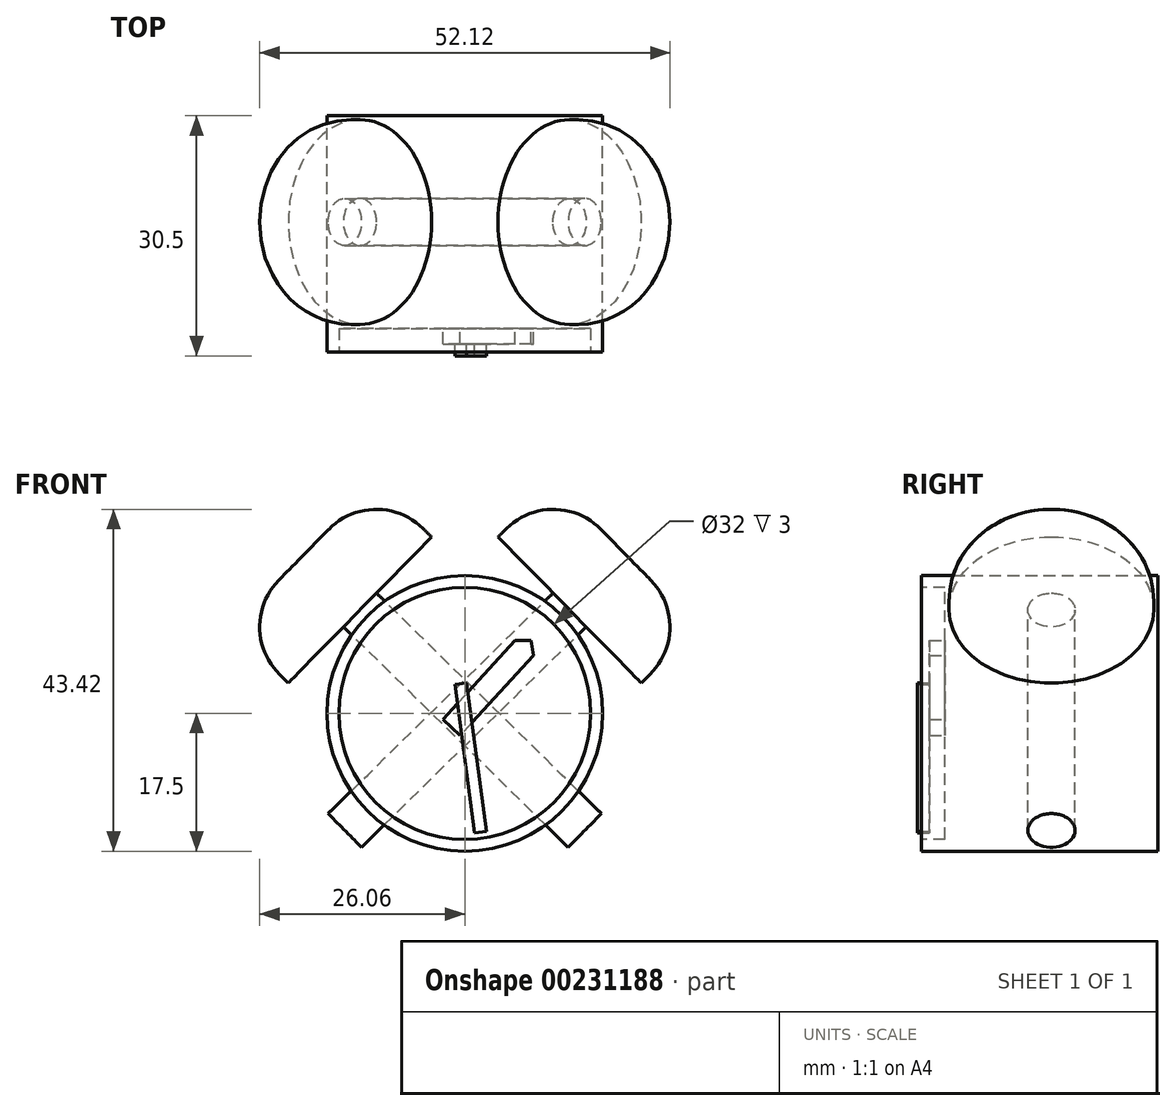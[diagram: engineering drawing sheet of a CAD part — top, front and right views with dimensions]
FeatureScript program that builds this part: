
annotation { "Feature Type Name" : "Feature", "Feature Type Description" : "" }
export const myFeature = defineFeature(function(context is Context, id is Id, definition is map)
    precondition{}
    {
        {
            var Q0;
            Q0=qCreatedBy(makeId("Front.planeOp"),FACE);
            var sketch = newSketch(context, id + "F0", { "sketchPlane" : qUnion([Q0])});
            skCircle(sketch, "E0", {"center": v(0, 0) * mm, "radius": 17.5 * mm});
            skSolve(sketch);
        }
        {
            var Q0;
            Q0=makeQuery(id+"F0.imprint","IMPRINT",FACE,{"disambiguationData":[TD([[makeQuery(id+"F0.imprint","IMPRINT",EDGE,{"derivedFrom":sQuery(id+"F0.wireOp",EDGE,"E0")}),1.0]])]});
            extrude(context, id + "F1", {"entities" : qUnion([Q0]), "depth" : 30 * mm});
        }
        {
            var Q0;
            Q0=makeQuery(id+"F1.opExtrude","CAP_FACE",FACE,{"disambiguationData":[OSD([sQuery(id+"F0.wireOp",EDGE,"E0")])],"isStart":false});
            var sketch = newSketch(context, id + "F2", { "sketchPlane" : qUnion([Q0])});
            skCircle(sketch, "E1", {"center": v(0, 0) * mm, "radius": 16 * mm});
            skSolve(sketch);
        }
        {
            var Q0;
            Q0=makeQuery(id+"F2.imprint","IMPRINT",FACE,{"disambiguationData":[TD([[makeQuery(id+"F2.imprint","IMPRINT",EDGE,{"derivedFrom":sQuery(id+"F2.wireOp",EDGE,"E1")}),1.0]])]});
            extrude(context, id + "F3", {"entities" : qUnion([Q0]), "operationType" : NewBodyOperationType.REMOVE, "oppositeDirection" : true, "depth" : 3 * mm});
        }
        {
            var Q0;
            Q0=makeQuery(id+"F1.opExtrude","CAP_FACE",FACE,{"disambiguationData":[OSD([sQuery(id+"F0.wireOp",EDGE,"E0")])],"isStart":true});
            var Q1;
            Q1=makeQuery(id+"F3.boolean.opBoolean","COPY",FACE,{"derivedFrom":makeQuery(id+"F3.opExtrude","CAP_FACE",FACE,{"disambiguationData":[OSD([sQuery(id+"F2.wireOp",EDGE,"E1")])],"isStart":false})});
            cPlane(context, id + "F4", {"entities" : qUnion([Q0, Q1]), "cplaneType" : CPlaneType.MID_PLANE, "offset" : 25 * mm, "width" : 150 * mm, "height" : 150 * mm});
        }
        {
            var Q0;
            Q0=qCreatedBy(id+"F4.planeOp",FACE);
            var sketch = newSketch(context, id + "F5", { "sketchPlane" : qUnion([Q0])});
            skLineSegment(sketch, "E2", {"start": v(20.46, 20.14) * mm, "end": v(-15.24, -14.87) * mm});
            skLineSegment(sketch, "E3", {"start": v(-15.24, -14.87) * mm, "end": v(-17.34, -12.73) * mm});
            skLineSegment(sketch, "E4", {"start": v(-17.34, -12.73) * mm, "end": v(18.36, 22.28) * mm});
            skLineSegment(sketch, "E5", {"start": v(18.36, 22.28) * mm, "end": v(20.46, 20.14) * mm});
            skLineSegment(sketch, "E6", {"start": v(18.36, 22.28) * mm, "end": v(11.35, 29.42) * mm});
            skLineSegment(sketch, "E7", {"start": v(11.35, 29.42) * mm, "end": v(4.21, 22.42) * mm});
            skLineSegment(sketch, "E8", {"start": v(4.21, 22.42) * mm, "end": v(11.35, 15.14) * mm});
            skSolve(sketch);
        }
        {
            var Q0;
            {var subQ0=sQuery(id+"F5.wireOp",EDGE,"E6");Q0=makeQuery(id+"F5.imprint","IMPRINT",FACE,{"disambiguationData":[TD([[makeQuery(id+"F5.imprint","IMPRINT",EDGE,{"derivedFrom":subQ0}),1.0]])]});}
            var Q1;
            Q1=makeQuery(id+"F5.imprint","IMPRINT",FACE,{"disambiguationData":[TD([[makeQuery(id+"F5.imprint","IMPRINT",EDGE,{"derivedFrom":sQuery(id+"F5.wireOp",EDGE,"E2")}),-1.0]])]});
            var Q2;
            Q2=sQuery(id+"F5.wireOp",EDGE,"E2");
            revolve(context, id + "F6", {"entities" : qUnion([Q0, Q1]), "axis" : qUnion([Q2]), "revolveType" : RevolveType.FULL});
        }
        {
            var Q0;
            Q0=makeQuery(id+"F6.opRevolve","SWEPT_EDGE",EDGE,{"disambiguationData":[OSD([sQuery(id+"F5.wireOp",EDGE,"E6"),sQuery(id+"F5.wireOp",EDGE,"E7")])]});
            fillet(context, id + "F7", {"entities" : qUnion([Q0]), "radius" : 8.45 * mm, "tangentPropagation" : true, "allowEdgeOverflow" : false});
        }
        {
            var Q0;
            Q0=makeQuery(id+"F6.opRevolve","SWEPT_BODY",BODY,{"disambiguationData":[OSD([sQuery(id+"F5.wireOp",EDGE,"E2"),sQuery(id+"F5.wireOp",EDGE,"E3"),sQuery(id+"F5.wireOp",EDGE,"E4"),sQuery(id+"F5.wireOp",EDGE,"E5"),sQuery(id+"F5.wireOp",EDGE,"E6"),sQuery(id+"F5.wireOp",EDGE,"E7"),sQuery(id+"F5.wireOp",EDGE,"E8")])]});
            var Q1;
            Q1=qCreatedBy(makeId("Right.planeOp"),FACE);
            mirror(context, id + "F8", {"entities" : qUnion([Q0]), "mirrorPlane" : qUnion([Q1])});
        }
        {
            var Q0;
            Q0=makeQuery(id+"F3.boolean.opBoolean","COPY",FACE,{"derivedFrom":makeQuery(id+"F3.opExtrude","CAP_FACE",FACE,{"disambiguationData":[OSD([sQuery(id+"F2.wireOp",EDGE,"E1")])],"isStart":false})});
            var sketch = newSketch(context, id + "F9", { "sketchPlane" : qUnion([Q0])});
            skLineSegment(sketch, "E9", {"start": v(-2.8, -0.78) * mm, "end": v(6.4, 9.3) * mm});
            skLineSegment(sketch, "E10", {"start": v(8.71, 7.39) * mm, "end": v(-0.58, -2.8) * mm});
            skLineSegment(sketch, "E11", {"start": v(-0.58, -2.8) * mm, "end": v(-2.8, -0.78) * mm});
            skLineSegment(sketch, "E12", {"start": v(8.42, 9.3) * mm, "end": v(6.4, 9.3) * mm});
            skPoint(sketch, "E12.endSnap0", {"position": v(8.42, 9.3) * mm});
            skLineSegment(sketch, "E13", {"start": v(6.4, 9.3) * mm, "end": v(8.42, 9.3) * mm});
            skLineSegment(sketch, "E14", {"start": v(8.42, 9.3) * mm, "end": v(8.71, 7.39) * mm});
            skSolve(sketch);
        }
        {
            var Q0;
            Q0=makeQuery(id+"F9.imprint","IMPRINT",FACE,{"disambiguationData":[TD([[makeQuery(id+"F9.imprint","IMPRINT",EDGE,{"derivedFrom":sQuery(id+"F9.wireOp",EDGE,"E9")}),-1.0]])]});
            extrude(context, id + "F10", {"entities" : qUnion([Q0]), "depth" : 2 * mm});
        }
        {
            var Q0;
            Q0=makeQuery(id+"F10.opExtrude","CAP_FACE",FACE,{"disambiguationData":[OSD([sQuery(id+"F9.wireOp",EDGE,"E9"),sQuery(id+"F9.wireOp",EDGE,"E10"),sQuery(id+"F9.wireOp",EDGE,"E11"),sQuery(id+"F9.wireOp",EDGE,"E13"),sQuery(id+"F9.wireOp",EDGE,"E14")])],"isStart":false});
            var sketch = newSketch(context, id + "F11", { "sketchPlane" : qUnion([Q0])});
            skLineSegment(sketch, "E15", {"start": v(-1.25, 3.66) * mm, "end": v(1.25, -15.18) * mm});
            skLineSegment(sketch, "E16", {"start": v(1.25, -15.18) * mm, "end": v(2.74, -14.98) * mm});
            skLineSegment(sketch, "E17", {"start": v(2.74, -14.98) * mm, "end": v(0.24, 3.85) * mm});
            skLineSegment(sketch, "E18", {"start": v(0.24, 3.85) * mm, "end": v(-1.25, 3.66) * mm});
            skSolve(sketch);
        }
        {
            var Q0;
            {var subQ0=sQuery(id+"F11.wireOp",EDGE,"E16");Q0=makeQuery(id+"F11.imprint","IMPRINT",FACE,{"disambiguationData":[TD([[makeQuery(id+"F11.imprint","IMPRINT",EDGE,{"derivedFrom":subQ0}),1.0]])]});}
            var Q1;
            {var subQ0=sQuery(id+"F11.wireOp",EDGE,"E18");Q1=makeQuery(id+"F11.imprint","IMPRINT",FACE,{"disambiguationData":[TD([[makeQuery(id+"F11.imprint","IMPRINT",EDGE,{"derivedFrom":subQ0}),1.0]])]});}
            var Q2;
            {var subQ0=sQuery(id+"F11.wireOp",EDGE,"E15");var subQ1=makeQuery(id+"F10.opExtrude","CAP_EDGE",EDGE,{"disambiguationData":[OSD([sQuery(id+"F9.wireOp",EDGE,"E9")])],"isStart":false});var subQ2=makeQuery(id+"F11.imprint","INTERSECT",VERTEX,{"derivedFrom":[subQ1,subQ0]});Q2=makeQuery(id+"F11.imprint","IMPRINT",FACE,{"disambiguationData":[TD([[makeQuery(id+"F11.imprint","IMPRINT",EDGE,{"disambiguationData":[TD([[subQ2,-1.0]])],"derivedFrom":subQ0}),1.0]])]});}
            extrude(context, id + "F12", {"entities" : qUnion([Q0, Q1, Q2]), "depth" : 1.5 * mm});
        }
    });
